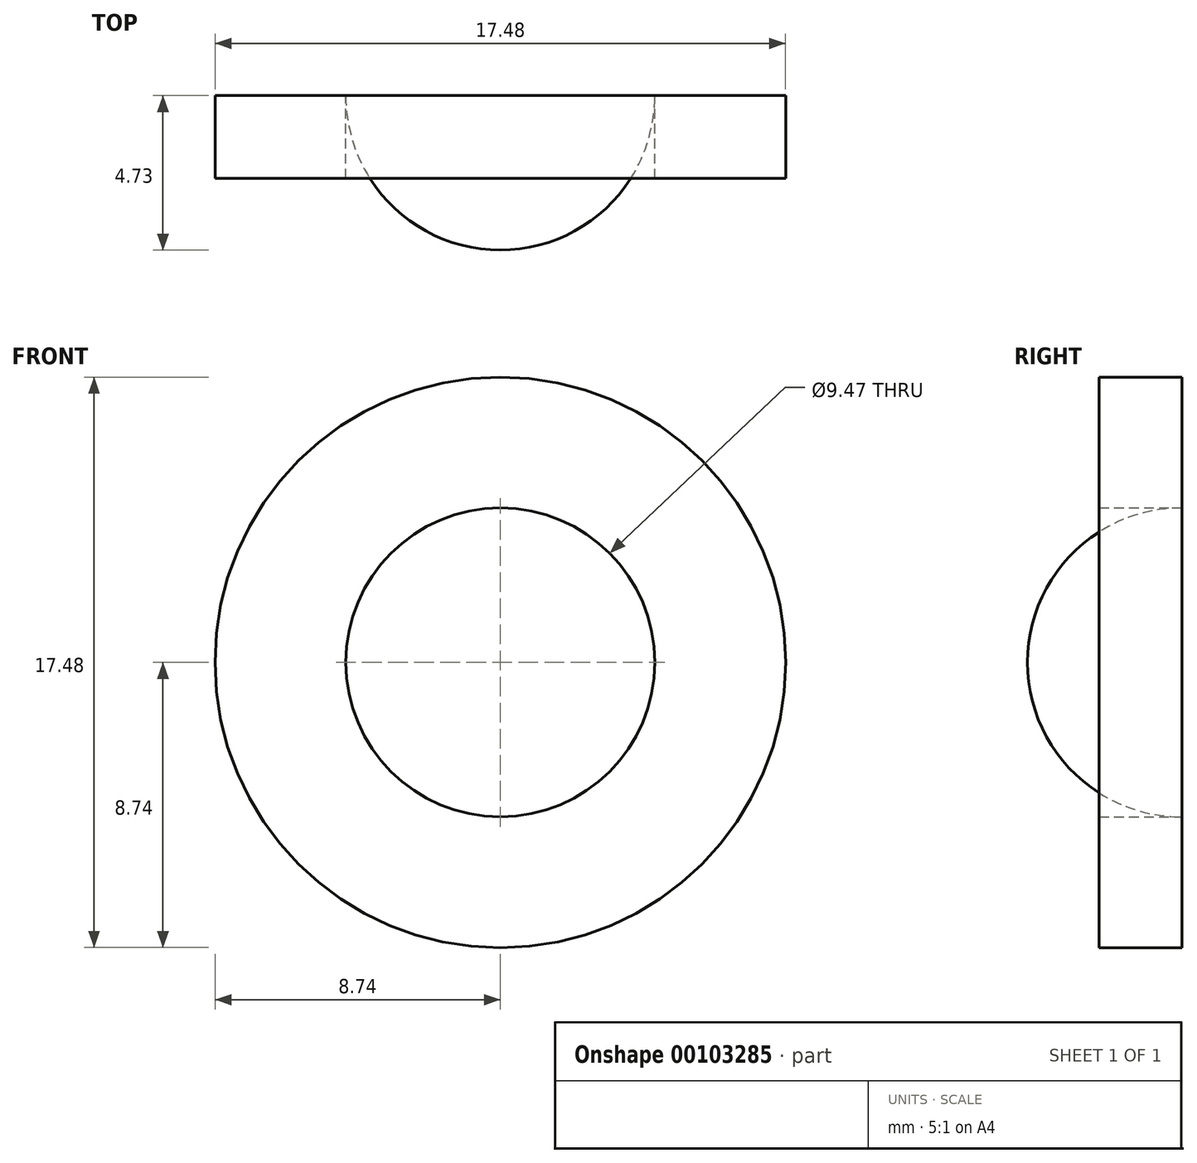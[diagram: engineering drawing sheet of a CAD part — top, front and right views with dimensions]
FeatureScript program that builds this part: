
annotation { "Feature Type Name" : "Feature", "Feature Type Description" : "" }
export const myFeature = defineFeature(function(context is Context, id is Id, definition is map)
    precondition{}
    {
        {
            var Q0;
            Q0=qCreatedBy(makeId("Front.planeOp"),FACE);
            var sketch = newSketch(context, id + "F0", { "sketchPlane" : qUnion([Q0])});
            skCircle(sketch, "E0", {"center": v(0, 0) * mm, "radius": 8.74 * mm});
            skCircle(sketch, "E1", {"center": v(0, 0) * mm, "radius": 4.73 * mm});
            skLineSegment(sketch, "E2", {"start": v(0, 4.73) * mm, "end": v(0, -4.73) * mm});
            skSolve(sketch);
        }
        {
            var Q0;
            Q0 = qSketchRegion(id + "F0", true);
            extrude(context, id + "F1", {"entities" : qUnion([Q0]), "depth" : 2.54 * mm});
        }
        {
            var Q0;
            {var subQ0=sQuery(id+"F0.wireOp",EDGE,"E2");Q0=makeQuery(id+"F0.imprint","IMPRINT",FACE,{"disambiguationData":[TD([[makeQuery(id+"F0.imprint","IMPRINT",EDGE,{"derivedFrom":subQ0}),-1.0]])]});}
            var Q1;
            Q1=sQuery(id+"F0.wireOp",EDGE,"E2");
            revolve(context, id + "F2", {"entities" : qUnion([Q0]), "axis" : qUnion([Q1]), "revolveType" : RevolveType.ONE_DIRECTION, "oppositeDirection" : true, "angle" : 180 * degree});
        }
    });
